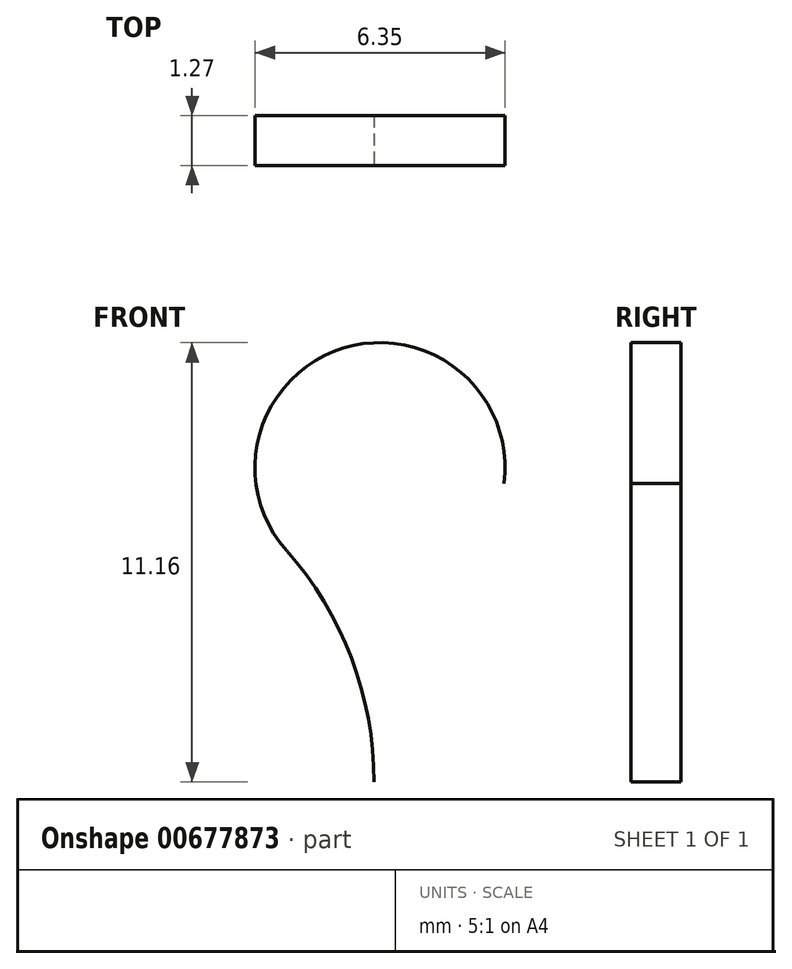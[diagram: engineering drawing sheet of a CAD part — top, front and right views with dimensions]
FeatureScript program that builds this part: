
annotation { "Feature Type Name" : "Feature", "Feature Type Description" : "" }
export const myFeature = defineFeature(function(context is Context, id is Id, definition is map)
    precondition{}
    {
        {
            var Q0;
            Q0=qCreatedBy(makeId("Front.planeOp"),FACE);
            var sketch = newSketch(context, id + "F0", { "sketchPlane" : qUnion([Q0])});
            skLineSegment(sketch, "E0", {"start": v(0, 0) * mm, "end": v(0, 3.17) * mm});
            skArc(sketch, "E1", {"start": v(3.3, 5.95) * mm, "mid": v(-1.89, 8.78) * mm, "end": v(0, 3.17) * mm});
            skSolve(sketch);
        }
        {
            var Q0;
            Q0=sQuery(id+"F0.wireOp",EDGE,"E0");
            var Q1;
            Q1=sQuery(id+"F0.wireOp",EDGE,"E1");
            extrude(context, id + "F1", {"bodyType" : ToolBodyType.SURFACE, "surfaceEntities" : qUnion([Q0, Q1]), "depth" : 1.27 * mm, "offsetDistance" : 25.4 * mm});
        }
        {
            var Q0;
            Q0=makeQuery(id+"F1.opExtrude","SWEPT_FACE",FACE,{"disambiguationData":[OSD([sQuery(id+"F0.wireOp",EDGE,"E1")])]});
            var Q1;
            Q1=makeQuery(id+"F1.opExtrude","SWEPT_EDGE",EDGE,{"disambiguationData":[OSD([sQuery(id+"F0.wireOp",VERTEX,"E1.end")])]});
            fillet(context, id + "F2", {"entities" : qUnion([Q0, Q1]), "radius" : 8.9 * mm, "tangentPropagation" : true, "allowEdgeOverflow" : false});
        }
    });
